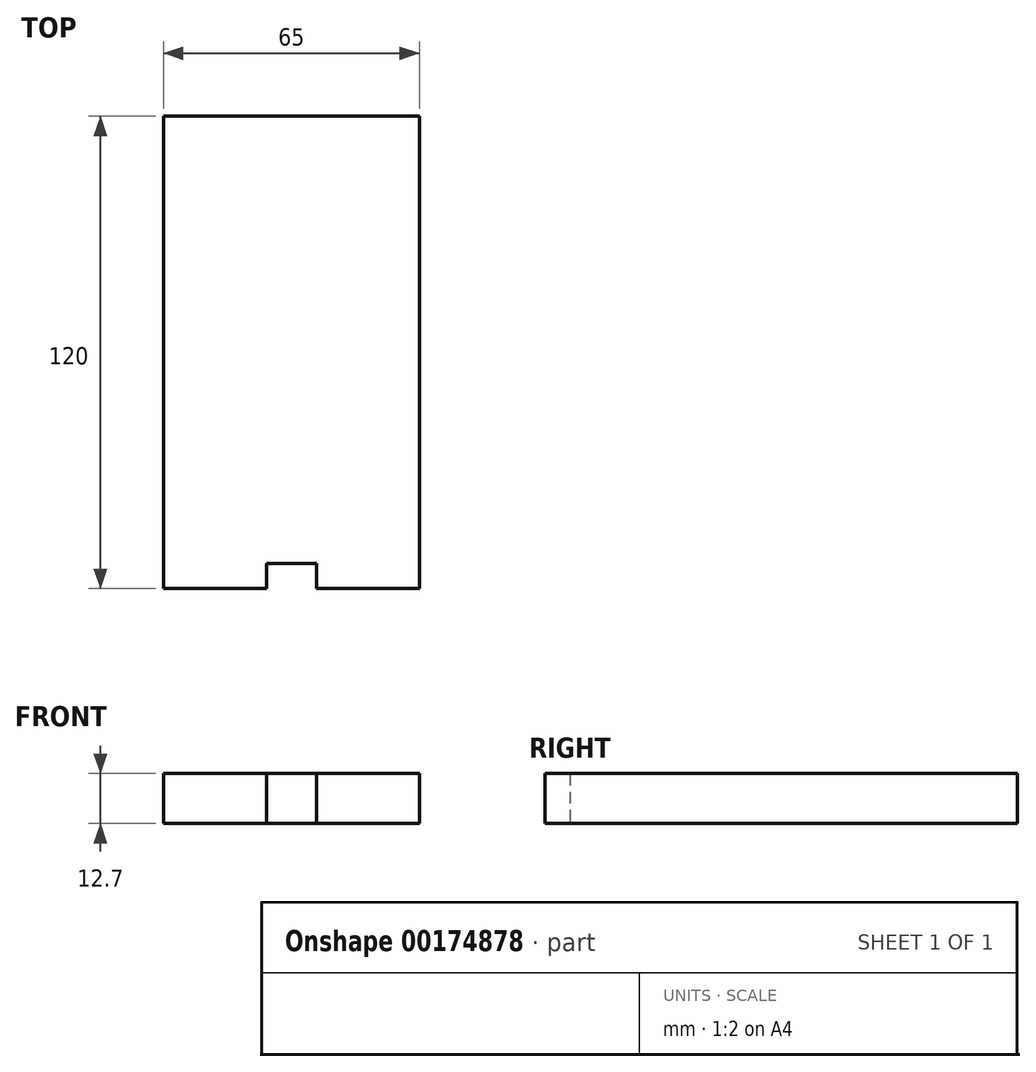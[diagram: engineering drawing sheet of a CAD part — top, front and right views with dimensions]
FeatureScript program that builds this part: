
annotation { "Feature Type Name" : "Feature", "Feature Type Description" : "" }
export const myFeature = defineFeature(function(context is Context, id is Id, definition is map)
    precondition{}
    {
        {
            var Q0;
            Q0=qCreatedBy(makeId("Top.planeOp"),FACE);
            var sketch = newSketch(context, id + "F0", { "sketchPlane" : qUnion([Q0])});
            skLineSegment(sketch, "E0.bottom", {"start": v(-32.5, -60) * mm, "end": v(32.5, -60) * mm});
            skLineSegment(sketch, "E0.top", {"start": v(-32.5, 60) * mm, "end": v(32.5, 60) * mm});
            skLineSegment(sketch, "E0.left", {"start": v(-32.5, -60) * mm, "end": v(-32.5, 60) * mm});
            skLineSegment(sketch, "E0.right", {"start": v(32.5, -60) * mm, "end": v(32.5, 60) * mm});
            skPoint(sketch, "E0.middle", {"position": v(0, 0) * mm});
            skLineSegment(sketch, "E1.bottom", {"start": v(6.35, -60) * mm, "end": v(-6.35, -60) * mm});
            skLineSegment(sketch, "E1.top", {"start": v(6.35, -53.65) * mm, "end": v(-6.35, -53.65) * mm});
            skLineSegment(sketch, "E1.left", {"start": v(6.35, -60) * mm, "end": v(6.35, -53.65) * mm});
            skLineSegment(sketch, "E1.right", {"start": v(-6.35, -60) * mm, "end": v(-6.35, -53.65) * mm});
            skPoint(sketch, "E1.middle", {"position": v(0, -56.83) * mm});
            skPoint(sketch, "E1.middle.positionSnap0", {"position": v(0, -60) * mm});
            skPoint(sketch, "E1.centerSnap0", {"position": v(0, -60) * mm});
            skSolve(sketch);
        }
        {
            var Q0;
            Q0=makeQuery(id+"F0.imprint","IMPRINT",FACE,{"disambiguationData":[TD([[makeQuery(id+"F0.imprint","IMPRINT",EDGE,{"derivedFrom":sQuery(id+"F0.wireOp",EDGE,"E0.bottom")}),1.0]])]});
            var Q1;
            Q1=makeQuery(id+"F0.imprint","IMPRINT",FACE,{"disambiguationData":[TD([[makeQuery(id+"F0.imprint","IMPRINT",EDGE,{"derivedFrom":sQuery(id+"F0.wireOp",EDGE,"E1.bottom")}),-1.0]])]});
            extrude(context, id + "F1", {"entities" : qUnion([Q0, Q1]), "depth" : 12.7 * mm});
        }
    });
